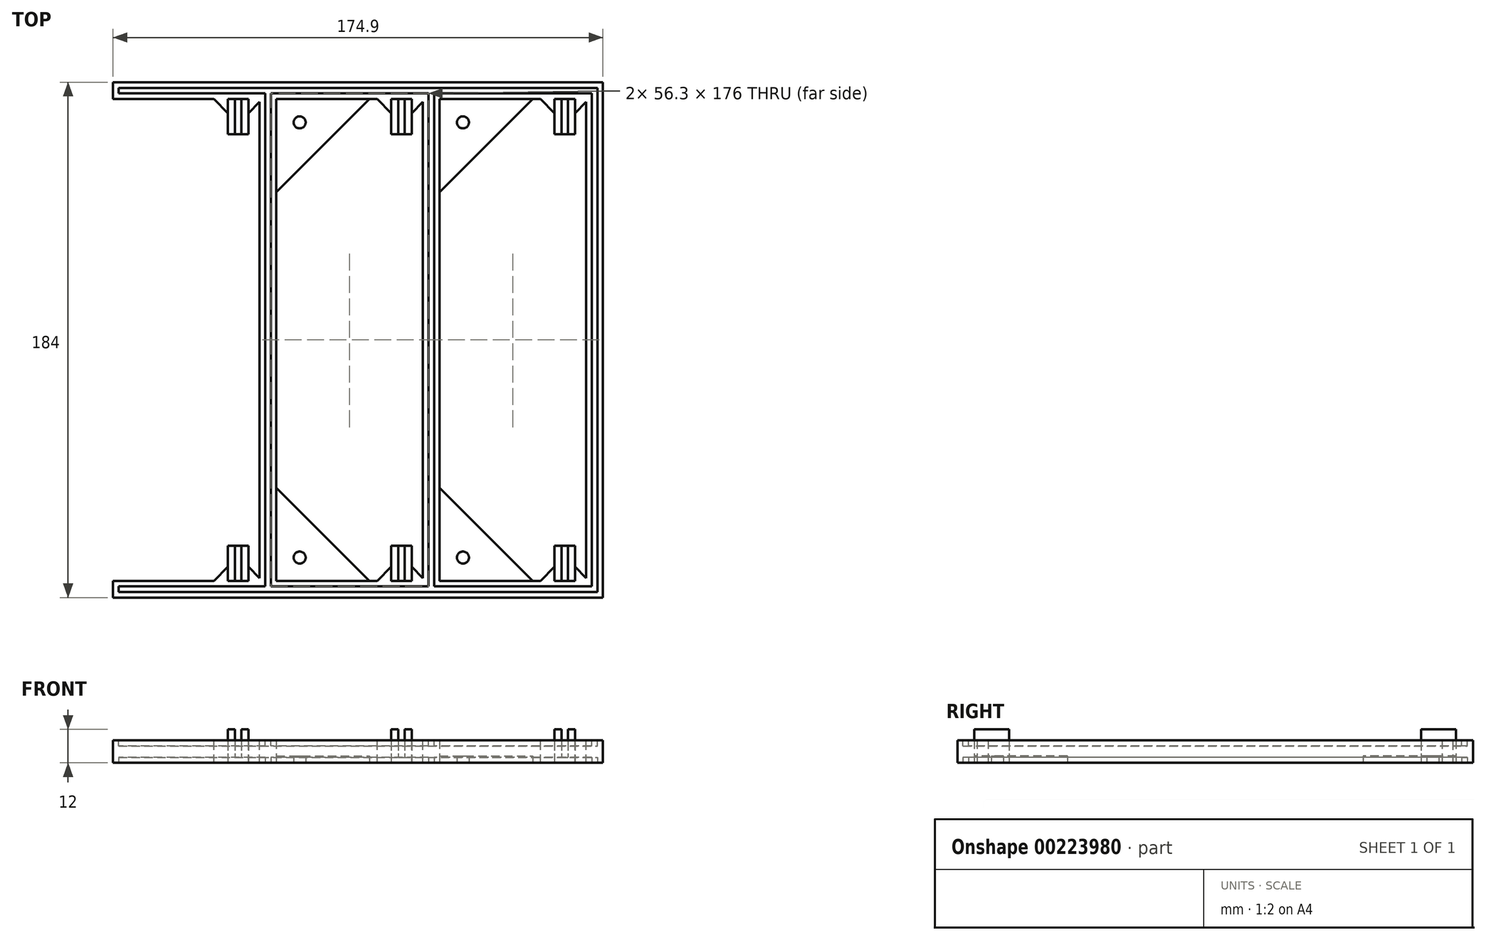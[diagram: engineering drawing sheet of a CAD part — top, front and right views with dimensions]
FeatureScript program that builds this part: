
annotation { "Feature Type Name" : "Feature", "Feature Type Description" : "" }
export const myFeature = defineFeature(function(context is Context, id is Id, definition is map)
    precondition{}
    {
        {
            var Q0;
            Q0=qCreatedBy(makeId("Top.planeOp"),FACE);
            var sketch = newSketch(context, id + "F0", { "sketchPlane" : qUnion([Q0])});
            skLineSegment(sketch, "E0", {"start": v(-87.45, 92) * mm, "end": v(87.45, 92) * mm});
            skLineSegment(sketch, "E1", {"start": v(-46.45, 73.5) * mm, "end": v(-43.95, 73.5) * mm});
            skLineSegment(sketch, "E2", {"start": v(-43.95, 73.5) * mm, "end": v(-43.95, 86) * mm});
            skLineSegment(sketch, "E3", {"start": v(-43.95, 86) * mm, "end": v(-41.65, 86) * mm});
            skLineSegment(sketch, "E4", {"start": v(-41.65, 86) * mm, "end": v(-41.65, 73.5) * mm});
            skLineSegment(sketch, "E5", {"start": v(-41.65, 73.5) * mm, "end": v(-39.15, 73.5) * mm});
            skLineSegment(sketch, "E6", {"start": v(-39.15, 73.5) * mm, "end": v(-39.15, 86) * mm});
            skLineSegment(sketch, "E7", {"start": v(-39.15, 86) * mm, "end": v(-35.15, 86) * mm});
            skLineSegment(sketch, "E8", {"start": v(-35.15, 86) * mm, "end": v(-35.15, 0) * mm});
            skLineSegment(sketch, "E9", {"start": v(-29.15, 0) * mm, "end": v(-29.15, 86) * mm});
            skLineSegment(sketch, "E10", {"start": v(-29.15, 86) * mm, "end": v(11.85, 86) * mm});
            skLineSegment(sketch, "E11", {"start": v(11.85, 86) * mm, "end": v(11.85, 73.5) * mm});
            skLineSegment(sketch, "E12", {"start": v(11.85, 73.5) * mm, "end": v(14.35, 73.5) * mm});
            skLineSegment(sketch, "E13", {"start": v(14.35, 73.5) * mm, "end": v(14.35, 86) * mm});
            skLineSegment(sketch, "E14", {"start": v(14.35, 86) * mm, "end": v(16.65, 86) * mm});
            skLineSegment(sketch, "E15", {"start": v(16.65, 86) * mm, "end": v(16.65, 73.5) * mm});
            skLineSegment(sketch, "E16", {"start": v(16.65, 73.5) * mm, "end": v(19.15, 73.5) * mm});
            skLineSegment(sketch, "E17", {"start": v(19.15, 73.5) * mm, "end": v(19.15, 86) * mm});
            skLineSegment(sketch, "E18", {"start": v(19.15, 86) * mm, "end": v(23.15, 86) * mm});
            skLineSegment(sketch, "E19", {"start": v(23.15, 86) * mm, "end": v(23.15, 0) * mm});
            skLineSegment(sketch, "E20", {"start": v(29.15, 0) * mm, "end": v(29.15, 86) * mm});
            skLineSegment(sketch, "E21", {"start": v(29.15, 86) * mm, "end": v(70.15, 86) * mm});
            skLineSegment(sketch, "E22", {"start": v(70.15, 86) * mm, "end": v(70.15, 73.5) * mm});
            skLineSegment(sketch, "E23", {"start": v(70.15, 73.5) * mm, "end": v(72.65, 73.5) * mm});
            skLineSegment(sketch, "E24", {"start": v(72.65, 73.5) * mm, "end": v(72.65, 86) * mm});
            skLineSegment(sketch, "E25", {"start": v(72.65, 86) * mm, "end": v(74.95, 86) * mm});
            skLineSegment(sketch, "E26", {"start": v(74.95, 86) * mm, "end": v(74.95, 73.5) * mm});
            skLineSegment(sketch, "E27", {"start": v(74.95, 73.5) * mm, "end": v(77.45, 73.5) * mm});
            skLineSegment(sketch, "E28", {"start": v(77.45, 73.5) * mm, "end": v(77.45, 86) * mm});
            skLineSegment(sketch, "E29", {"start": v(77.45, 86) * mm, "end": v(81.45, 86) * mm});
            skLineSegment(sketch, "E30", {"start": v(81.45, 86) * mm, "end": v(81.45, 0) * mm});
            skLineSegment(sketch, "E31", {"start": v(87.45, 0) * mm, "end": v(87.45, 92) * mm});
            skLineSegment(sketch, "E32", {"start": v(-8.65, 86) * mm, "end": v(-8.65, 92) * mm, "construction": true});
            skPoint(sketch, "E33", {"position": v(0, 92) * mm});
            skLineSegment(sketch, "E34", {"start": v(-35.15, 43) * mm, "end": v(-29.15, 43) * mm, "construction": true});
            skLineSegment(sketch, "E35", {"start": v(23.15, 43) * mm, "end": v(29.15, 43) * mm, "construction": true});
            skLineSegment(sketch, "E36", {"start": v(81.45, 43) * mm, "end": v(87.45, 43) * mm, "construction": true});
            skLineSegment(sketch, "E37", {"start": v(-46.45, 73.5) * mm, "end": v(-46.45, 86) * mm});
            skLineSegment(sketch, "E38", {"start": v(-46.45, 86) * mm, "end": v(-87.45, 86) * mm});
            skLineSegment(sketch, "E39", {"start": v(-87.45, 86) * mm, "end": v(-87.45, 92) * mm});
            skLineSegment(sketch, "E40.MirrorCS", {"start": v(74.95, -73.5) * mm, "end": v(77.45, -73.5) * mm});
            skLineSegment(sketch, "E41.MirrorCS", {"start": v(77.45, -86) * mm, "end": v(81.45, -86) * mm});
            skLineSegment(sketch, "E42.MirrorCS", {"start": v(19.15, -86) * mm, "end": v(23.15, -86) * mm});
            skLineSegment(sketch, "E43.MirrorCS", {"start": v(11.85, -73.5) * mm, "end": v(14.35, -73.5) * mm});
            skLineSegment(sketch, "E44.MirrorCS", {"start": v(70.15, -73.5) * mm, "end": v(72.65, -73.5) * mm});
            skLineSegment(sketch, "E45.MirrorCS", {"start": v(-46.45, -73.5) * mm, "end": v(-43.95, -73.5) * mm});
            skLineSegment(sketch, "E46.MirrorCS", {"start": v(-43.95, -86) * mm, "end": v(-41.65, -86) * mm});
            skLineSegment(sketch, "E47.MirrorCS", {"start": v(-41.65, -73.5) * mm, "end": v(-39.15, -73.5) * mm});
            skLineSegment(sketch, "E48.MirrorCS", {"start": v(-39.15, -86) * mm, "end": v(-35.15, -86) * mm});
            skLineSegment(sketch, "E49.MirrorCS", {"start": v(72.65, -86) * mm, "end": v(74.95, -86) * mm});
            skLineSegment(sketch, "E50.MirrorCS", {"start": v(16.65, -73.5) * mm, "end": v(19.15, -73.5) * mm});
            skLineSegment(sketch, "E51.MirrorCS", {"start": v(14.35, -86) * mm, "end": v(16.65, -86) * mm});
            skLineSegment(sketch, "E52.MirrorCS", {"start": v(29.15, -86) * mm, "end": v(70.15, -86) * mm});
            skLineSegment(sketch, "E53.MirrorCS", {"start": v(-46.45, -73.5) * mm, "end": v(-46.45, -86) * mm});
            skLineSegment(sketch, "E54.MirrorCS", {"start": v(19.15, -73.5) * mm, "end": v(19.15, -86) * mm});
            skLineSegment(sketch, "E55.MirrorCS", {"start": v(-43.95, -73.5) * mm, "end": v(-43.95, -86) * mm});
            skLineSegment(sketch, "E56.MirrorCS", {"start": v(87.45, 0) * mm, "end": v(87.45, -92) * mm});
            skLineSegment(sketch, "E57.MirrorCS", {"start": v(-87.45, -86) * mm, "end": v(-87.45, -92) * mm});
            skLineSegment(sketch, "E58.MirrorCS", {"start": v(29.15, 0) * mm, "end": v(29.15, -86) * mm});
            skPoint(sketch, "E59.MirrorP", {"position": v(0, -92) * mm});
            skLineSegment(sketch, "E60.MirrorCS", {"start": v(-8.65, -86) * mm, "end": v(-8.65, -92) * mm, "construction": true});
            skLineSegment(sketch, "E61.MirrorCS", {"start": v(72.65, -73.5) * mm, "end": v(72.65, -86) * mm});
            skLineSegment(sketch, "E62.MirrorCS", {"start": v(81.45, -86) * mm, "end": v(81.45, 0) * mm});
            skLineSegment(sketch, "E63.MirrorCS", {"start": v(23.15, -86) * mm, "end": v(23.15, 0) * mm});
            skLineSegment(sketch, "E64.MirrorCS", {"start": v(-46.45, -86) * mm, "end": v(-87.45, -86) * mm});
            skLineSegment(sketch, "E65.MirrorCS", {"start": v(-87.45, -92) * mm, "end": v(87.45, -92) * mm});
            skLineSegment(sketch, "E66.MirrorCS", {"start": v(70.15, -86) * mm, "end": v(70.15, -73.5) * mm});
            skLineSegment(sketch, "E67.MirrorCS", {"start": v(-41.65, -86) * mm, "end": v(-41.65, -73.5) * mm});
            skLineSegment(sketch, "E68.MirrorCS", {"start": v(-39.15, -73.5) * mm, "end": v(-39.15, -86) * mm});
            skLineSegment(sketch, "E69.MirrorCS", {"start": v(-35.15, -86) * mm, "end": v(-35.15, 0) * mm});
            skLineSegment(sketch, "E70.MirrorCS", {"start": v(-29.15, 0) * mm, "end": v(-29.15, -86) * mm});
            skLineSegment(sketch, "E71.MirrorCS", {"start": v(-29.15, -86) * mm, "end": v(11.85, -86) * mm});
            skLineSegment(sketch, "E72.MirrorCS", {"start": v(11.85, -86) * mm, "end": v(11.85, -73.5) * mm});
            skLineSegment(sketch, "E73.MirrorCS", {"start": v(77.45, -73.5) * mm, "end": v(77.45, -86) * mm});
            skLineSegment(sketch, "E74.MirrorCS", {"start": v(74.95, -86) * mm, "end": v(74.95, -73.5) * mm});
            skLineSegment(sketch, "E75.MirrorCS", {"start": v(14.35, -73.5) * mm, "end": v(14.35, -86) * mm});
            skLineSegment(sketch, "E76.MirrorCS", {"start": v(16.65, -86) * mm, "end": v(16.65, -73.5) * mm});
            skSolve(sketch);
        }
        {
            var Q0;
            Q0=qSketchRegion(id+"F0",true);
            extrude(context, id + "F1", {"entities" : qUnion([Q0]), "depth" : 8 * mm});
        }
        {
            var Q0;
            Q0=makeQuery(id+"F1.opExtrude","CAP_FACE",FACE,{"disambiguationData":[OSD([sQuery(id+"F0.wireOp",EDGE,"E0"),sQuery(id+"F0.wireOp",EDGE,"E1"),sQuery(id+"F0.wireOp",EDGE,"E2"),sQuery(id+"F0.wireOp",EDGE,"E3"),sQuery(id+"F0.wireOp",EDGE,"E4"),sQuery(id+"F0.wireOp",EDGE,"E5"),sQuery(id+"F0.wireOp",EDGE,"E6"),sQuery(id+"F0.wireOp",EDGE,"E7"),sQuery(id+"F0.wireOp",EDGE,"E8"),sQuery(id+"F0.wireOp",EDGE,"E9"),sQuery(id+"F0.wireOp",EDGE,"E10"),sQuery(id+"F0.wireOp",EDGE,"E11"),sQuery(id+"F0.wireOp",EDGE,"E12"),sQuery(id+"F0.wireOp",EDGE,"E13"),sQuery(id+"F0.wireOp",EDGE,"E14"),sQuery(id+"F0.wireOp",EDGE,"E15"),sQuery(id+"F0.wireOp",EDGE,"E16"),sQuery(id+"F0.wireOp",EDGE,"E17"),sQuery(id+"F0.wireOp",EDGE,"E18"),sQuery(id+"F0.wireOp",EDGE,"E19"),sQuery(id+"F0.wireOp",EDGE,"E20"),sQuery(id+"F0.wireOp",EDGE,"E21"),sQuery(id+"F0.wireOp",EDGE,"E22"),sQuery(id+"F0.wireOp",EDGE,"E23"),sQuery(id+"F0.wireOp",EDGE,"E24"),sQuery(id+"F0.wireOp",EDGE,"E25"),sQuery(id+"F0.wireOp",EDGE,"E26"),sQuery(id+"F0.wireOp",EDGE,"E27"),sQuery(id+"F0.wireOp",EDGE,"E28"),sQuery(id+"F0.wireOp",EDGE,"E29"),sQuery(id+"F0.wireOp",EDGE,"E30"),sQuery(id+"F0.wireOp",EDGE,"E31"),sQuery(id+"F0.wireOp",EDGE,"E37"),sQuery(id+"F0.wireOp",EDGE,"E38"),sQuery(id+"F0.wireOp",EDGE,"E39"),sQuery(id+"F0.wireOp",EDGE,"E40.MirrorCS"),sQuery(id+"F0.wireOp",EDGE,"E41.MirrorCS"),sQuery(id+"F0.wireOp",EDGE,"E42.MirrorCS"),sQuery(id+"F0.wireOp",EDGE,"E43.MirrorCS"),sQuery(id+"F0.wireOp",EDGE,"E44.MirrorCS"),sQuery(id+"F0.wireOp",EDGE,"E45.MirrorCS"),sQuery(id+"F0.wireOp",EDGE,"E46.MirrorCS"),sQuery(id+"F0.wireOp",EDGE,"E47.MirrorCS"),sQuery(id+"F0.wireOp",EDGE,"E48.MirrorCS"),sQuery(id+"F0.wireOp",EDGE,"E49.MirrorCS"),sQuery(id+"F0.wireOp",EDGE,"E50.MirrorCS"),sQuery(id+"F0.wireOp",EDGE,"E51.MirrorCS"),sQuery(id+"F0.wireOp",EDGE,"E52.MirrorCS"),sQuery(id+"F0.wireOp",EDGE,"E53.MirrorCS"),sQuery(id+"F0.wireOp",EDGE,"E54.MirrorCS"),sQuery(id+"F0.wireOp",EDGE,"E55.MirrorCS"),sQuery(id+"F0.wireOp",EDGE,"E56.MirrorCS"),sQuery(id+"F0.wireOp",EDGE,"E57.MirrorCS"),sQuery(id+"F0.wireOp",EDGE,"E58.MirrorCS"),sQuery(id+"F0.wireOp",EDGE,"E61.MirrorCS"),sQuery(id+"F0.wireOp",EDGE,"E62.MirrorCS"),sQuery(id+"F0.wireOp",EDGE,"E63.MirrorCS"),sQuery(id+"F0.wireOp",EDGE,"E64.MirrorCS"),sQuery(id+"F0.wireOp",EDGE,"E65.MirrorCS"),sQuery(id+"F0.wireOp",EDGE,"E66.MirrorCS"),sQuery(id+"F0.wireOp",EDGE,"E67.MirrorCS"),sQuery(id+"F0.wireOp",EDGE,"E68.MirrorCS"),sQuery(id+"F0.wireOp",EDGE,"E69.MirrorCS"),sQuery(id+"F0.wireOp",EDGE,"E70.MirrorCS"),sQuery(id+"F0.wireOp",EDGE,"E71.MirrorCS"),sQuery(id+"F0.wireOp",EDGE,"E72.MirrorCS"),sQuery(id+"F0.wireOp",EDGE,"E73.MirrorCS"),sQuery(id+"F0.wireOp",EDGE,"E74.MirrorCS"),sQuery(id+"F0.wireOp",EDGE,"E75.MirrorCS"),sQuery(id+"F0.wireOp",EDGE,"E76.MirrorCS")])],"isStart":false});
            var sketch = newSketch(context, id + "F2", { "sketchPlane" : qUnion([Q0])});
            skLineSegment(sketch, "E77.0", {"start": v(-46.45, 73.5) * mm, "end": v(-46.45, 86) * mm});
            skLineSegment(sketch, "E77.1", {"start": v(-46.45, 73.5) * mm, "end": v(-43.95, 73.5) * mm});
            skLineSegment(sketch, "E77.2", {"start": v(-43.95, 73.5) * mm, "end": v(-43.95, 86) * mm});
            skLineSegment(sketch, "E77.3", {"start": v(-41.65, 86) * mm, "end": v(-41.65, 73.5) * mm});
            skLineSegment(sketch, "E77.4", {"start": v(-41.65, 73.5) * mm, "end": v(-39.15, 73.5) * mm});
            skLineSegment(sketch, "E77.5", {"start": v(-39.15, 73.5) * mm, "end": v(-39.15, 86) * mm});
            skLineSegment(sketch, "E77.6", {"start": v(-43.95, 86) * mm, "end": v(-41.65, 86) * mm});
            skLineSegment(sketch, "E77.7", {"start": v(11.85, 86) * mm, "end": v(11.85, 73.5) * mm});
            skLineSegment(sketch, "E77.8", {"start": v(14.35, 73.5) * mm, "end": v(14.35, 86) * mm});
            skLineSegment(sketch, "E77.9", {"start": v(16.65, 86) * mm, "end": v(16.65, 73.5) * mm});
            skLineSegment(sketch, "E77.10", {"start": v(14.35, 86) * mm, "end": v(16.65, 86) * mm});
            skLineSegment(sketch, "E77.11", {"start": v(19.15, 73.5) * mm, "end": v(19.15, 86) * mm});
            skLineSegment(sketch, "E77.12", {"start": v(16.65, 73.5) * mm, "end": v(19.15, 73.5) * mm});
            skLineSegment(sketch, "E77.13", {"start": v(11.85, 73.5) * mm, "end": v(14.35, 73.5) * mm});
            skLineSegment(sketch, "E77.14", {"start": v(77.45, 73.5) * mm, "end": v(77.45, 86) * mm});
            skLineSegment(sketch, "E77.15", {"start": v(74.95, 73.5) * mm, "end": v(77.45, 73.5) * mm});
            skLineSegment(sketch, "E77.16", {"start": v(74.95, 86) * mm, "end": v(74.95, 73.5) * mm});
            skLineSegment(sketch, "E77.17", {"start": v(72.65, 86) * mm, "end": v(74.95, 86) * mm});
            skLineSegment(sketch, "E77.18", {"start": v(72.65, 73.5) * mm, "end": v(72.65, 86) * mm});
            skLineSegment(sketch, "E77.19", {"start": v(70.15, 73.5) * mm, "end": v(72.65, 73.5) * mm});
            skLineSegment(sketch, "E77.20", {"start": v(70.15, 86) * mm, "end": v(70.15, 73.5) * mm});
            skLineSegment(sketch, "E78", {"start": v(-46.45, 86) * mm, "end": v(-43.95, 86) * mm});
            skLineSegment(sketch, "E79", {"start": v(-41.65, 86) * mm, "end": v(-39.15, 86) * mm});
            skLineSegment(sketch, "E80", {"start": v(11.85, 86) * mm, "end": v(14.35, 86) * mm});
            skLineSegment(sketch, "E81", {"start": v(16.65, 86) * mm, "end": v(19.15, 86) * mm});
            skLineSegment(sketch, "E82", {"start": v(70.15, 86) * mm, "end": v(72.65, 86) * mm});
            skLineSegment(sketch, "E83", {"start": v(74.95, 86) * mm, "end": v(77.45, 86) * mm});
            skLineSegment(sketch, "E84.MirrorCS", {"start": v(72.65, -86) * mm, "end": v(74.95, -86) * mm});
            skLineSegment(sketch, "E85.MirrorCS", {"start": v(-43.95, -86) * mm, "end": v(-41.65, -86) * mm});
            skLineSegment(sketch, "E86.MirrorCS", {"start": v(14.35, -86) * mm, "end": v(16.65, -86) * mm});
            skLineSegment(sketch, "E87.MirrorCS", {"start": v(70.15, -73.5) * mm, "end": v(72.65, -73.5) * mm});
            skLineSegment(sketch, "E88.MirrorCS", {"start": v(74.95, -73.5) * mm, "end": v(77.45, -73.5) * mm});
            skLineSegment(sketch, "E89.MirrorCS", {"start": v(-41.65, -73.5) * mm, "end": v(-39.15, -73.5) * mm});
            skLineSegment(sketch, "E90.MirrorCS", {"start": v(16.65, -86) * mm, "end": v(19.15, -86) * mm});
            skLineSegment(sketch, "E91.MirrorCS", {"start": v(-46.45, -86) * mm, "end": v(-43.95, -86) * mm});
            skLineSegment(sketch, "E92.MirrorCS", {"start": v(16.65, -73.5) * mm, "end": v(19.15, -73.5) * mm});
            skLineSegment(sketch, "E93.MirrorCS", {"start": v(11.85, -86) * mm, "end": v(14.35, -86) * mm});
            skLineSegment(sketch, "E94.MirrorCS", {"start": v(74.95, -86) * mm, "end": v(77.45, -86) * mm});
            skLineSegment(sketch, "E95.MirrorCS", {"start": v(-46.45, -73.5) * mm, "end": v(-43.95, -73.5) * mm});
            skLineSegment(sketch, "E96.MirrorCS", {"start": v(-41.65, -86) * mm, "end": v(-39.15, -86) * mm});
            skLineSegment(sketch, "E97.MirrorCS", {"start": v(70.15, -86) * mm, "end": v(72.65, -86) * mm});
            skLineSegment(sketch, "E98.MirrorCS", {"start": v(11.85, -73.5) * mm, "end": v(14.35, -73.5) * mm});
            skLineSegment(sketch, "E99.MirrorCS", {"start": v(72.65, -73.5) * mm, "end": v(72.65, -86) * mm});
            skLineSegment(sketch, "E100.MirrorCS", {"start": v(70.15, -86) * mm, "end": v(70.15, -73.5) * mm});
            skLineSegment(sketch, "E101.MirrorCS", {"start": v(77.45, -73.5) * mm, "end": v(77.45, -86) * mm});
            skLineSegment(sketch, "E102.MirrorCS", {"start": v(11.85, -86) * mm, "end": v(11.85, -73.5) * mm});
            skLineSegment(sketch, "E103.MirrorCS", {"start": v(-46.45, -73.5) * mm, "end": v(-46.45, -86) * mm});
            skLineSegment(sketch, "E104.MirrorCS", {"start": v(-43.95, -73.5) * mm, "end": v(-43.95, -86) * mm});
            skLineSegment(sketch, "E105.MirrorCS", {"start": v(74.95, -86) * mm, "end": v(74.95, -73.5) * mm});
            skLineSegment(sketch, "E106.MirrorCS", {"start": v(-41.65, -86) * mm, "end": v(-41.65, -73.5) * mm});
            skLineSegment(sketch, "E107.MirrorCS", {"start": v(14.35, -73.5) * mm, "end": v(14.35, -86) * mm});
            skLineSegment(sketch, "E108.MirrorCS", {"start": v(-39.15, -73.5) * mm, "end": v(-39.15, -86) * mm});
            skLineSegment(sketch, "E109.MirrorCS", {"start": v(19.15, -73.5) * mm, "end": v(19.15, -86) * mm});
            skLineSegment(sketch, "E110.MirrorCS", {"start": v(16.65, -86) * mm, "end": v(16.65, -73.5) * mm});
            skSolve(sketch);
        }
        {
            var Q0;
            Q0=qSketchRegion(id+"F2",true);
            extrude(context, id + "F3", {"entities" : qUnion([Q0]), "operationType" : NewBodyOperationType.ADD, "depth" : 4 * mm});
        }
        {
            var Q0;
            Q0=makeQuery(id+"F1.opExtrude","CAP_FACE",FACE,{"disambiguationData":[OSD([sQuery(id+"F0.wireOp",EDGE,"E0"),sQuery(id+"F0.wireOp",EDGE,"E1"),sQuery(id+"F0.wireOp",EDGE,"E2"),sQuery(id+"F0.wireOp",EDGE,"E3"),sQuery(id+"F0.wireOp",EDGE,"E4"),sQuery(id+"F0.wireOp",EDGE,"E5"),sQuery(id+"F0.wireOp",EDGE,"E6"),sQuery(id+"F0.wireOp",EDGE,"E7"),sQuery(id+"F0.wireOp",EDGE,"E8"),sQuery(id+"F0.wireOp",EDGE,"E9"),sQuery(id+"F0.wireOp",EDGE,"E10"),sQuery(id+"F0.wireOp",EDGE,"E11"),sQuery(id+"F0.wireOp",EDGE,"E12"),sQuery(id+"F0.wireOp",EDGE,"E13"),sQuery(id+"F0.wireOp",EDGE,"E14"),sQuery(id+"F0.wireOp",EDGE,"E15"),sQuery(id+"F0.wireOp",EDGE,"E16"),sQuery(id+"F0.wireOp",EDGE,"E17"),sQuery(id+"F0.wireOp",EDGE,"E18"),sQuery(id+"F0.wireOp",EDGE,"E19"),sQuery(id+"F0.wireOp",EDGE,"E20"),sQuery(id+"F0.wireOp",EDGE,"E21"),sQuery(id+"F0.wireOp",EDGE,"E22"),sQuery(id+"F0.wireOp",EDGE,"E23"),sQuery(id+"F0.wireOp",EDGE,"E24"),sQuery(id+"F0.wireOp",EDGE,"E25"),sQuery(id+"F0.wireOp",EDGE,"E26"),sQuery(id+"F0.wireOp",EDGE,"E27"),sQuery(id+"F0.wireOp",EDGE,"E28"),sQuery(id+"F0.wireOp",EDGE,"E29"),sQuery(id+"F0.wireOp",EDGE,"E30"),sQuery(id+"F0.wireOp",EDGE,"E31"),sQuery(id+"F0.wireOp",EDGE,"E37"),sQuery(id+"F0.wireOp",EDGE,"E38"),sQuery(id+"F0.wireOp",EDGE,"E39"),sQuery(id+"F0.wireOp",EDGE,"E40.MirrorCS"),sQuery(id+"F0.wireOp",EDGE,"E41.MirrorCS"),sQuery(id+"F0.wireOp",EDGE,"E42.MirrorCS"),sQuery(id+"F0.wireOp",EDGE,"E43.MirrorCS"),sQuery(id+"F0.wireOp",EDGE,"E44.MirrorCS"),sQuery(id+"F0.wireOp",EDGE,"E45.MirrorCS"),sQuery(id+"F0.wireOp",EDGE,"E46.MirrorCS"),sQuery(id+"F0.wireOp",EDGE,"E47.MirrorCS"),sQuery(id+"F0.wireOp",EDGE,"E48.MirrorCS"),sQuery(id+"F0.wireOp",EDGE,"E49.MirrorCS"),sQuery(id+"F0.wireOp",EDGE,"E50.MirrorCS"),sQuery(id+"F0.wireOp",EDGE,"E51.MirrorCS"),sQuery(id+"F0.wireOp",EDGE,"E52.MirrorCS"),sQuery(id+"F0.wireOp",EDGE,"E53.MirrorCS"),sQuery(id+"F0.wireOp",EDGE,"E54.MirrorCS"),sQuery(id+"F0.wireOp",EDGE,"E55.MirrorCS"),sQuery(id+"F0.wireOp",EDGE,"E56.MirrorCS"),sQuery(id+"F0.wireOp",EDGE,"E57.MirrorCS"),sQuery(id+"F0.wireOp",EDGE,"E58.MirrorCS"),sQuery(id+"F0.wireOp",EDGE,"E61.MirrorCS"),sQuery(id+"F0.wireOp",EDGE,"E62.MirrorCS"),sQuery(id+"F0.wireOp",EDGE,"E63.MirrorCS"),sQuery(id+"F0.wireOp",EDGE,"E64.MirrorCS"),sQuery(id+"F0.wireOp",EDGE,"E65.MirrorCS"),sQuery(id+"F0.wireOp",EDGE,"E66.MirrorCS"),sQuery(id+"F0.wireOp",EDGE,"E67.MirrorCS"),sQuery(id+"F0.wireOp",EDGE,"E68.MirrorCS"),sQuery(id+"F0.wireOp",EDGE,"E69.MirrorCS"),sQuery(id+"F0.wireOp",EDGE,"E70.MirrorCS"),sQuery(id+"F0.wireOp",EDGE,"E71.MirrorCS"),sQuery(id+"F0.wireOp",EDGE,"E72.MirrorCS"),sQuery(id+"F0.wireOp",EDGE,"E73.MirrorCS"),sQuery(id+"F0.wireOp",EDGE,"E74.MirrorCS"),sQuery(id+"F0.wireOp",EDGE,"E75.MirrorCS"),sQuery(id+"F0.wireOp",EDGE,"E76.MirrorCS")])],"isStart":true});
            var sketch = newSketch(context, id + "F4", { "sketchPlane" : qUnion([Q0])});
            skLineSegment(sketch, "E111.bottom", {"start": v(-46.45, 73.5) * mm, "end": v(-39.15, 73.5) * mm});
            skLineSegment(sketch, "E111.top", {"start": v(-46.45, 86) * mm, "end": v(-39.15, 86) * mm});
            skLineSegment(sketch, "E111.left", {"start": v(-46.45, 73.5) * mm, "end": v(-46.45, 86) * mm});
            skLineSegment(sketch, "E111.right", {"start": v(-39.15, 73.5) * mm, "end": v(-39.15, 86) * mm});
            skLineSegment(sketch, "E112.bottom", {"start": v(11.85, 73.5) * mm, "end": v(19.15, 73.5) * mm});
            skLineSegment(sketch, "E112.top", {"start": v(11.85, 86) * mm, "end": v(19.15, 86) * mm});
            skLineSegment(sketch, "E112.left", {"start": v(11.85, 73.5) * mm, "end": v(11.85, 86) * mm});
            skLineSegment(sketch, "E112.right", {"start": v(19.15, 73.5) * mm, "end": v(19.15, 86) * mm});
            skLineSegment(sketch, "E113.bottom", {"start": v(70.15, 73.5) * mm, "end": v(77.45, 73.5) * mm});
            skLineSegment(sketch, "E113.top", {"start": v(70.15, 86) * mm, "end": v(77.45, 86) * mm});
            skLineSegment(sketch, "E113.left", {"start": v(70.15, 73.5) * mm, "end": v(70.15, 86) * mm});
            skLineSegment(sketch, "E113.right", {"start": v(77.45, 73.5) * mm, "end": v(77.45, 86) * mm});
            skLineSegment(sketch, "E114.MirrorCS", {"start": v(11.85, -86) * mm, "end": v(19.15, -86) * mm});
            skLineSegment(sketch, "E115.MirrorCS", {"start": v(11.85, -73.5) * mm, "end": v(19.15, -73.5) * mm});
            skLineSegment(sketch, "E116.MirrorCS", {"start": v(-39.15, -73.5) * mm, "end": v(-39.15, -86) * mm});
            skLineSegment(sketch, "E117.MirrorCS", {"start": v(11.85, -73.5) * mm, "end": v(11.85, -86) * mm});
            skLineSegment(sketch, "E118.MirrorCS", {"start": v(70.15, -73.5) * mm, "end": v(70.15, -86) * mm});
            skLineSegment(sketch, "E119.MirrorCS", {"start": v(77.45, -73.5) * mm, "end": v(77.45, -86) * mm});
            skLineSegment(sketch, "E120.MirrorCS", {"start": v(19.15, -73.5) * mm, "end": v(19.15, -86) * mm});
            skLineSegment(sketch, "E121.MirrorCS", {"start": v(70.15, -86) * mm, "end": v(77.45, -86) * mm});
            skLineSegment(sketch, "E122.MirrorCS", {"start": v(-46.45, -73.5) * mm, "end": v(-46.45, -86) * mm});
            skLineSegment(sketch, "E123.MirrorCS", {"start": v(-46.45, -73.5) * mm, "end": v(-39.15, -73.5) * mm});
            skLineSegment(sketch, "E124.MirrorCS", {"start": v(-46.45, -86) * mm, "end": v(-39.15, -86) * mm});
            skLineSegment(sketch, "E125.MirrorCS", {"start": v(70.15, -73.5) * mm, "end": v(77.45, -73.5) * mm});
            skSolve(sketch);
        }
        {
            var Q0;
            Q0=qSketchRegion(id+"F4",true);
            extrude(context, id + "F5", {"entities" : qUnion([Q0]), "operationType" : NewBodyOperationType.ADD, "oppositeDirection" : true, "depth" : 2 * mm});
        }
        {
            var Q0;
            Q0=makeQuery(id+"F1.opExtrude","CAP_FACE",FACE,{"disambiguationData":[OSD([sQuery(id+"F0.wireOp",EDGE,"E0"),sQuery(id+"F0.wireOp",EDGE,"E1"),sQuery(id+"F0.wireOp",EDGE,"E2"),sQuery(id+"F0.wireOp",EDGE,"E3"),sQuery(id+"F0.wireOp",EDGE,"E4"),sQuery(id+"F0.wireOp",EDGE,"E5"),sQuery(id+"F0.wireOp",EDGE,"E6"),sQuery(id+"F0.wireOp",EDGE,"E7"),sQuery(id+"F0.wireOp",EDGE,"E8"),sQuery(id+"F0.wireOp",EDGE,"E9"),sQuery(id+"F0.wireOp",EDGE,"E10"),sQuery(id+"F0.wireOp",EDGE,"E11"),sQuery(id+"F0.wireOp",EDGE,"E12"),sQuery(id+"F0.wireOp",EDGE,"E13"),sQuery(id+"F0.wireOp",EDGE,"E14"),sQuery(id+"F0.wireOp",EDGE,"E15"),sQuery(id+"F0.wireOp",EDGE,"E16"),sQuery(id+"F0.wireOp",EDGE,"E17"),sQuery(id+"F0.wireOp",EDGE,"E18"),sQuery(id+"F0.wireOp",EDGE,"E19"),sQuery(id+"F0.wireOp",EDGE,"E20"),sQuery(id+"F0.wireOp",EDGE,"E21"),sQuery(id+"F0.wireOp",EDGE,"E22"),sQuery(id+"F0.wireOp",EDGE,"E23"),sQuery(id+"F0.wireOp",EDGE,"E24"),sQuery(id+"F0.wireOp",EDGE,"E25"),sQuery(id+"F0.wireOp",EDGE,"E26"),sQuery(id+"F0.wireOp",EDGE,"E27"),sQuery(id+"F0.wireOp",EDGE,"E28"),sQuery(id+"F0.wireOp",EDGE,"E29"),sQuery(id+"F0.wireOp",EDGE,"E30"),sQuery(id+"F0.wireOp",EDGE,"E31"),sQuery(id+"F0.wireOp",EDGE,"E37"),sQuery(id+"F0.wireOp",EDGE,"E38"),sQuery(id+"F0.wireOp",EDGE,"E39"),sQuery(id+"F0.wireOp",EDGE,"E40.MirrorCS"),sQuery(id+"F0.wireOp",EDGE,"E41.MirrorCS"),sQuery(id+"F0.wireOp",EDGE,"E42.MirrorCS"),sQuery(id+"F0.wireOp",EDGE,"E43.MirrorCS"),sQuery(id+"F0.wireOp",EDGE,"E44.MirrorCS"),sQuery(id+"F0.wireOp",EDGE,"E45.MirrorCS"),sQuery(id+"F0.wireOp",EDGE,"E46.MirrorCS"),sQuery(id+"F0.wireOp",EDGE,"E47.MirrorCS"),sQuery(id+"F0.wireOp",EDGE,"E48.MirrorCS"),sQuery(id+"F0.wireOp",EDGE,"E49.MirrorCS"),sQuery(id+"F0.wireOp",EDGE,"E50.MirrorCS"),sQuery(id+"F0.wireOp",EDGE,"E51.MirrorCS"),sQuery(id+"F0.wireOp",EDGE,"E52.MirrorCS"),sQuery(id+"F0.wireOp",EDGE,"E53.MirrorCS"),sQuery(id+"F0.wireOp",EDGE,"E54.MirrorCS"),sQuery(id+"F0.wireOp",EDGE,"E55.MirrorCS"),sQuery(id+"F0.wireOp",EDGE,"E56.MirrorCS"),sQuery(id+"F0.wireOp",EDGE,"E57.MirrorCS"),sQuery(id+"F0.wireOp",EDGE,"E58.MirrorCS"),sQuery(id+"F0.wireOp",EDGE,"E61.MirrorCS"),sQuery(id+"F0.wireOp",EDGE,"E62.MirrorCS"),sQuery(id+"F0.wireOp",EDGE,"E63.MirrorCS"),sQuery(id+"F0.wireOp",EDGE,"E64.MirrorCS"),sQuery(id+"F0.wireOp",EDGE,"E65.MirrorCS"),sQuery(id+"F0.wireOp",EDGE,"E66.MirrorCS"),sQuery(id+"F0.wireOp",EDGE,"E67.MirrorCS"),sQuery(id+"F0.wireOp",EDGE,"E68.MirrorCS"),sQuery(id+"F0.wireOp",EDGE,"E69.MirrorCS"),sQuery(id+"F0.wireOp",EDGE,"E70.MirrorCS"),sQuery(id+"F0.wireOp",EDGE,"E71.MirrorCS"),sQuery(id+"F0.wireOp",EDGE,"E72.MirrorCS"),sQuery(id+"F0.wireOp",EDGE,"E73.MirrorCS"),sQuery(id+"F0.wireOp",EDGE,"E74.MirrorCS"),sQuery(id+"F0.wireOp",EDGE,"E75.MirrorCS"),sQuery(id+"F0.wireOp",EDGE,"E76.MirrorCS")])],"isStart":false});
            var sketch = newSketch(context, id + "F6", { "sketchPlane" : qUnion([Q0])});
            skLineSegment(sketch, "E126", {"start": v(-85.45, 90) * mm, "end": v(85.45, 90) * mm});
            skLineSegment(sketch, "E127", {"start": v(85.45, 90) * mm, "end": v(85.45, 0) * mm});
            skPoint(sketch, "E127.endSnap0", {"position": v(81.45, 0) * mm});
            skLineSegment(sketch, "E128", {"start": v(83.45, 88) * mm, "end": v(83.45, 0) * mm});
            skLineSegment(sketch, "E129", {"start": v(83.45, 88) * mm, "end": v(27.15, 88) * mm});
            skLineSegment(sketch, "E130", {"start": v(27.15, 88) * mm, "end": v(27.15, 0) * mm});
            skPoint(sketch, "E130.endSnap0", {"position": v(29.15, 0) * mm});
            skLineSegment(sketch, "E131", {"start": v(25.15, 0) * mm, "end": v(25.15, 88) * mm});
            skLineSegment(sketch, "E132", {"start": v(25.15, 88) * mm, "end": v(-31.15, 88) * mm});
            skLineSegment(sketch, "E133", {"start": v(-31.15, 88) * mm, "end": v(-31.15, 0) * mm});
            skPoint(sketch, "E133.endSnap0", {"position": v(-29.15, 0) * mm});
            skLineSegment(sketch, "E134", {"start": v(-33.15, 0) * mm, "end": v(-33.15, 88) * mm});
            skLineSegment(sketch, "E135", {"start": v(-33.15, 88) * mm, "end": v(-85.45, 88) * mm});
            skLineSegment(sketch, "E136", {"start": v(-85.45, 90) * mm, "end": v(-85.45, 88) * mm});
            skLineSegment(sketch, "E137", {"start": v(-33.15, 44) * mm, "end": v(-31.15, 44) * mm, "construction": true});
            skLineSegment(sketch, "E138", {"start": v(25.15, 44) * mm, "end": v(27.15, 44) * mm, "construction": true});
            skLineSegment(sketch, "E139", {"start": v(83.45, 44) * mm, "end": v(85.45, 44) * mm, "construction": true});
            skLineSegment(sketch, "E140", {"start": v(0, 90) * mm, "end": v(0, 92) * mm, "construction": true});
            skLineSegment(sketch, "E141", {"start": v(27.15, 44) * mm, "end": v(29.15, 44) * mm, "construction": true});
            skLineSegment(sketch, "E142", {"start": v(85.45, 44) * mm, "end": v(87.45, 44) * mm, "construction": true});
            skLineSegment(sketch, "E143", {"start": v(-31.15, 44) * mm, "end": v(-29.15, 44) * mm, "construction": true});
            skLineSegment(sketch, "E144", {"start": v(-85.45, 89) * mm, "end": v(-87.45, 89) * mm, "construction": true});
            skLineSegment(sketch, "E145.MirrorCS", {"start": v(85.45, -44) * mm, "end": v(87.45, -44) * mm, "construction": true});
            skLineSegment(sketch, "E146.MirrorCS", {"start": v(-85.45, -90) * mm, "end": v(-85.45, -88) * mm});
            skLineSegment(sketch, "E147.MirrorCS", {"start": v(-85.45, -89) * mm, "end": v(-87.45, -89) * mm, "construction": true});
            skLineSegment(sketch, "E148.MirrorCS", {"start": v(-31.15, -44) * mm, "end": v(-29.15, -44) * mm, "construction": true});
            skLineSegment(sketch, "E149.MirrorCS", {"start": v(25.15, -44) * mm, "end": v(27.15, -44) * mm, "construction": true});
            skLineSegment(sketch, "E150.MirrorCS", {"start": v(27.15, -44) * mm, "end": v(29.15, -44) * mm, "construction": true});
            skLineSegment(sketch, "E151.MirrorCS", {"start": v(0, -90) * mm, "end": v(0, -92) * mm, "construction": true});
            skLineSegment(sketch, "E152.MirrorCS", {"start": v(-33.15, -44) * mm, "end": v(-31.15, -44) * mm, "construction": true});
            skLineSegment(sketch, "E153.MirrorCS", {"start": v(83.45, -44) * mm, "end": v(85.45, -44) * mm, "construction": true});
            skLineSegment(sketch, "E154.MirrorCS", {"start": v(27.15, -88) * mm, "end": v(27.15, 0) * mm});
            skLineSegment(sketch, "E155.MirrorCS", {"start": v(83.45, -88) * mm, "end": v(27.15, -88) * mm});
            skLineSegment(sketch, "E156.MirrorCS", {"start": v(25.15, 0) * mm, "end": v(25.15, -88) * mm});
            skLineSegment(sketch, "E157.MirrorCS", {"start": v(25.15, -88) * mm, "end": v(-31.15, -88) * mm});
            skLineSegment(sketch, "E158.MirrorCS", {"start": v(83.45, -88) * mm, "end": v(83.45, 0) * mm});
            skLineSegment(sketch, "E159.MirrorCS", {"start": v(-31.15, -88) * mm, "end": v(-31.15, 0) * mm});
            skLineSegment(sketch, "E160.MirrorCS", {"start": v(-33.15, 0) * mm, "end": v(-33.15, -88) * mm});
            skLineSegment(sketch, "E161.MirrorCS", {"start": v(85.45, -90) * mm, "end": v(85.45, 0) * mm});
            skLineSegment(sketch, "E162.MirrorCS", {"start": v(-85.45, -90) * mm, "end": v(85.45, -90) * mm});
            skLineSegment(sketch, "E163.MirrorCS", {"start": v(-33.15, -88) * mm, "end": v(-85.45, -88) * mm});
            skSolve(sketch);
        }
        {
            var Q0;
            Q0=qSketchRegion(id+"F6",true);
            extrude(context, id + "F7", {"entities" : qUnion([Q0]), "operationType" : NewBodyOperationType.REMOVE, "oppositeDirection" : true, "depth" : 2 * mm});
        }
        {
            var Q0;
            Q0=makeQuery(id+"F1.opExtrude","CAP_FACE",FACE,{"disambiguationData":[OSD([sQuery(id+"F0.wireOp",EDGE,"E0"),sQuery(id+"F0.wireOp",EDGE,"E1"),sQuery(id+"F0.wireOp",EDGE,"E2"),sQuery(id+"F0.wireOp",EDGE,"E3"),sQuery(id+"F0.wireOp",EDGE,"E4"),sQuery(id+"F0.wireOp",EDGE,"E5"),sQuery(id+"F0.wireOp",EDGE,"E6"),sQuery(id+"F0.wireOp",EDGE,"E7"),sQuery(id+"F0.wireOp",EDGE,"E8"),sQuery(id+"F0.wireOp",EDGE,"E9"),sQuery(id+"F0.wireOp",EDGE,"E10"),sQuery(id+"F0.wireOp",EDGE,"E11"),sQuery(id+"F0.wireOp",EDGE,"E12"),sQuery(id+"F0.wireOp",EDGE,"E13"),sQuery(id+"F0.wireOp",EDGE,"E14"),sQuery(id+"F0.wireOp",EDGE,"E15"),sQuery(id+"F0.wireOp",EDGE,"E16"),sQuery(id+"F0.wireOp",EDGE,"E17"),sQuery(id+"F0.wireOp",EDGE,"E18"),sQuery(id+"F0.wireOp",EDGE,"E19"),sQuery(id+"F0.wireOp",EDGE,"E20"),sQuery(id+"F0.wireOp",EDGE,"E21"),sQuery(id+"F0.wireOp",EDGE,"E22"),sQuery(id+"F0.wireOp",EDGE,"E23"),sQuery(id+"F0.wireOp",EDGE,"E24"),sQuery(id+"F0.wireOp",EDGE,"E25"),sQuery(id+"F0.wireOp",EDGE,"E26"),sQuery(id+"F0.wireOp",EDGE,"E27"),sQuery(id+"F0.wireOp",EDGE,"E28"),sQuery(id+"F0.wireOp",EDGE,"E29"),sQuery(id+"F0.wireOp",EDGE,"E30"),sQuery(id+"F0.wireOp",EDGE,"E31"),sQuery(id+"F0.wireOp",EDGE,"E37"),sQuery(id+"F0.wireOp",EDGE,"E38"),sQuery(id+"F0.wireOp",EDGE,"E39"),sQuery(id+"F0.wireOp",EDGE,"E40.MirrorCS"),sQuery(id+"F0.wireOp",EDGE,"E41.MirrorCS"),sQuery(id+"F0.wireOp",EDGE,"E42.MirrorCS"),sQuery(id+"F0.wireOp",EDGE,"E43.MirrorCS"),sQuery(id+"F0.wireOp",EDGE,"E44.MirrorCS"),sQuery(id+"F0.wireOp",EDGE,"E45.MirrorCS"),sQuery(id+"F0.wireOp",EDGE,"E46.MirrorCS"),sQuery(id+"F0.wireOp",EDGE,"E47.MirrorCS"),sQuery(id+"F0.wireOp",EDGE,"E48.MirrorCS"),sQuery(id+"F0.wireOp",EDGE,"E49.MirrorCS"),sQuery(id+"F0.wireOp",EDGE,"E50.MirrorCS"),sQuery(id+"F0.wireOp",EDGE,"E51.MirrorCS"),sQuery(id+"F0.wireOp",EDGE,"E52.MirrorCS"),sQuery(id+"F0.wireOp",EDGE,"E53.MirrorCS"),sQuery(id+"F0.wireOp",EDGE,"E54.MirrorCS"),sQuery(id+"F0.wireOp",EDGE,"E55.MirrorCS"),sQuery(id+"F0.wireOp",EDGE,"E56.MirrorCS"),sQuery(id+"F0.wireOp",EDGE,"E57.MirrorCS"),sQuery(id+"F0.wireOp",EDGE,"E58.MirrorCS"),sQuery(id+"F0.wireOp",EDGE,"E61.MirrorCS"),sQuery(id+"F0.wireOp",EDGE,"E62.MirrorCS"),sQuery(id+"F0.wireOp",EDGE,"E63.MirrorCS"),sQuery(id+"F0.wireOp",EDGE,"E64.MirrorCS"),sQuery(id+"F0.wireOp",EDGE,"E65.MirrorCS"),sQuery(id+"F0.wireOp",EDGE,"E66.MirrorCS"),sQuery(id+"F0.wireOp",EDGE,"E67.MirrorCS"),sQuery(id+"F0.wireOp",EDGE,"E68.MirrorCS"),sQuery(id+"F0.wireOp",EDGE,"E69.MirrorCS"),sQuery(id+"F0.wireOp",EDGE,"E70.MirrorCS"),sQuery(id+"F0.wireOp",EDGE,"E71.MirrorCS"),sQuery(id+"F0.wireOp",EDGE,"E72.MirrorCS"),sQuery(id+"F0.wireOp",EDGE,"E73.MirrorCS"),sQuery(id+"F0.wireOp",EDGE,"E74.MirrorCS"),sQuery(id+"F0.wireOp",EDGE,"E75.MirrorCS"),sQuery(id+"F0.wireOp",EDGE,"E76.MirrorCS")])],"isStart":true});
            var sketch = newSketch(context, id + "F8", { "sketchPlane" : qUnion([Q0])});
            skLineSegment(sketch, "E164", {"start": v(-85.45, 90) * mm, "end": v(85.45, 90) * mm});
            skLineSegment(sketch, "E165", {"start": v(85.45, 90) * mm, "end": v(85.45, 0) * mm});
            skPoint(sketch, "E165.endSnap0", {"position": v(81.45, 0) * mm});
            skLineSegment(sketch, "E166", {"start": v(83.45, 88) * mm, "end": v(83.45, 0) * mm});
            skLineSegment(sketch, "E167", {"start": v(83.45, 88) * mm, "end": v(27.15, 88) * mm});
            skLineSegment(sketch, "E168", {"start": v(27.15, 88) * mm, "end": v(27.15, 0) * mm});
            skLineSegment(sketch, "E169", {"start": v(25.15, 0) * mm, "end": v(25.15, 88) * mm});
            skLineSegment(sketch, "E170", {"start": v(25.15, 88) * mm, "end": v(-31.15, 88) * mm});
            skLineSegment(sketch, "E171", {"start": v(-31.15, 88) * mm, "end": v(-31.15, 0) * mm});
            skLineSegment(sketch, "E172", {"start": v(-33.15, 0) * mm, "end": v(-33.15, 88) * mm});
            skLineSegment(sketch, "E173", {"start": v(-33.15, 88) * mm, "end": v(-85.45, 88) * mm});
            skLineSegment(sketch, "E174", {"start": v(-85.45, 88) * mm, "end": v(-85.45, 90) * mm});
            skLineSegment(sketch, "E175", {"start": v(-85.45, 89) * mm, "end": v(-87.45, 89) * mm, "construction": true});
            skLineSegment(sketch, "E176", {"start": v(0, 92) * mm, "end": v(0, 90) * mm, "construction": true});
            skLineSegment(sketch, "E177", {"start": v(0, 90) * mm, "end": v(0, 88) * mm, "construction": true});
            skLineSegment(sketch, "E178", {"start": v(-33.15, 44) * mm, "end": v(-31.15, 44) * mm, "construction": true});
            skLineSegment(sketch, "E179", {"start": v(-31.15, 44) * mm, "end": v(-29.15, 44) * mm, "construction": true});
            skLineSegment(sketch, "E180", {"start": v(25.15, 44) * mm, "end": v(27.15, 44) * mm, "construction": true});
            skLineSegment(sketch, "E181", {"start": v(27.15, 44) * mm, "end": v(29.15, 44) * mm, "construction": true});
            skLineSegment(sketch, "E182", {"start": v(83.45, 44) * mm, "end": v(85.45, 44) * mm, "construction": true});
            skLineSegment(sketch, "E183", {"start": v(85.45, 44) * mm, "end": v(87.45, 44) * mm, "construction": true});
            skLineSegment(sketch, "E184.MirrorCS", {"start": v(-33.15, -44) * mm, "end": v(-31.15, -44) * mm, "construction": true});
            skLineSegment(sketch, "E185.MirrorCS", {"start": v(0, -90) * mm, "end": v(0, -88) * mm, "construction": true});
            skLineSegment(sketch, "E186.MirrorCS", {"start": v(85.45, -44) * mm, "end": v(87.45, -44) * mm, "construction": true});
            skLineSegment(sketch, "E187.MirrorCS", {"start": v(25.15, -44) * mm, "end": v(27.15, -44) * mm, "construction": true});
            skLineSegment(sketch, "E188.MirrorCS", {"start": v(-85.45, -88) * mm, "end": v(-85.45, -90) * mm});
            skLineSegment(sketch, "E189.MirrorCS", {"start": v(-31.15, -44) * mm, "end": v(-29.15, -44) * mm, "construction": true});
            skLineSegment(sketch, "E190.MirrorCS", {"start": v(27.15, -44) * mm, "end": v(29.15, -44) * mm, "construction": true});
            skLineSegment(sketch, "E191.MirrorCS", {"start": v(83.45, -44) * mm, "end": v(85.45, -44) * mm, "construction": true});
            skLineSegment(sketch, "E192.MirrorCS", {"start": v(0, -92) * mm, "end": v(0, -90) * mm, "construction": true});
            skLineSegment(sketch, "E193.MirrorCS", {"start": v(-85.45, -89) * mm, "end": v(-87.45, -89) * mm, "construction": true});
            skLineSegment(sketch, "E194.MirrorCS", {"start": v(85.45, -90) * mm, "end": v(85.45, 0) * mm});
            skLineSegment(sketch, "E195.MirrorCS", {"start": v(-33.15, -88) * mm, "end": v(-85.45, -88) * mm});
            skLineSegment(sketch, "E196.MirrorCS", {"start": v(25.15, -88) * mm, "end": v(-31.15, -88) * mm});
            skLineSegment(sketch, "E197.MirrorCS", {"start": v(25.15, 0) * mm, "end": v(25.15, -88) * mm});
            skLineSegment(sketch, "E198.MirrorCS", {"start": v(-85.45, -90) * mm, "end": v(85.45, -90) * mm});
            skLineSegment(sketch, "E199.MirrorCS", {"start": v(-31.15, -88) * mm, "end": v(-31.15, 0) * mm});
            skLineSegment(sketch, "E200.MirrorCS", {"start": v(-33.15, 0) * mm, "end": v(-33.15, -88) * mm});
            skLineSegment(sketch, "E201.MirrorCS", {"start": v(83.45, -88) * mm, "end": v(27.15, -88) * mm});
            skLineSegment(sketch, "E202.MirrorCS", {"start": v(83.45, -88) * mm, "end": v(83.45, 0) * mm});
            skLineSegment(sketch, "E203.MirrorCS", {"start": v(27.15, -88) * mm, "end": v(27.15, 0) * mm});
            skSolve(sketch);
        }
        {
            var Q0;
            Q0=qSketchRegion(id+"F8",true);
            extrude(context, id + "F9", {"entities" : qUnion([Q0]), "operationType" : NewBodyOperationType.REMOVE, "oppositeDirection" : true, "depth" : 2 * mm});
        }
        {
            var Q0;
            Q0=makeQuery(id+"F1.opExtrude","SWEPT_EDGE",EDGE,{"disambiguationData":[OSD([sQuery(id+"F0.wireOp",EDGE,"E6"),sQuery(id+"F0.wireOp",EDGE,"E7")])]});
            var Q1;
            Q1=makeQuery(id+"F1.opExtrude","SWEPT_EDGE",EDGE,{"disambiguationData":[OSD([sQuery(id+"F0.wireOp",EDGE,"E37"),sQuery(id+"F0.wireOp",EDGE,"E38")])]});
            var Q2;
            Q2=makeQuery(id+"F1.opExtrude","SWEPT_EDGE",EDGE,{"disambiguationData":[OSD([sQuery(id+"F0.wireOp",EDGE,"E10"),sQuery(id+"F0.wireOp",EDGE,"E11")])]});
            var Q3;
            Q3=makeQuery(id+"F1.opExtrude","SWEPT_EDGE",EDGE,{"disambiguationData":[OSD([sQuery(id+"F0.wireOp",EDGE,"E17"),sQuery(id+"F0.wireOp",EDGE,"E18")])]});
            var Q4;
            Q4=makeQuery(id+"F1.opExtrude","SWEPT_EDGE",EDGE,{"disambiguationData":[OSD([sQuery(id+"F0.wireOp",EDGE,"E28"),sQuery(id+"F0.wireOp",EDGE,"E29")])]});
            var Q5;
            Q5=makeQuery(id+"F1.opExtrude","SWEPT_EDGE",EDGE,{"disambiguationData":[OSD([sQuery(id+"F0.wireOp",EDGE,"E21"),sQuery(id+"F0.wireOp",EDGE,"E22")])]});
            var Q6;
            Q6=makeQuery(id+"F1.opExtrude","SWEPT_EDGE",EDGE,{"disambiguationData":[OSD([sQuery(id+"F0.wireOp",EDGE,"E41.MirrorCS"),sQuery(id+"F0.wireOp",EDGE,"E73.MirrorCS")])]});
            var Q7;
            Q7=makeQuery(id+"F1.opExtrude","SWEPT_EDGE",EDGE,{"disambiguationData":[OSD([sQuery(id+"F0.wireOp",EDGE,"E52.MirrorCS"),sQuery(id+"F0.wireOp",EDGE,"E66.MirrorCS")])]});
            var Q8;
            Q8=makeQuery(id+"F1.opExtrude","SWEPT_EDGE",EDGE,{"disambiguationData":[OSD([sQuery(id+"F0.wireOp",EDGE,"E71.MirrorCS"),sQuery(id+"F0.wireOp",EDGE,"E72.MirrorCS")])]});
            var Q9;
            Q9=makeQuery(id+"F1.opExtrude","SWEPT_EDGE",EDGE,{"disambiguationData":[OSD([sQuery(id+"F0.wireOp",EDGE,"E53.MirrorCS"),sQuery(id+"F0.wireOp",EDGE,"E64.MirrorCS")])]});
            var Q10;
            Q10=makeQuery(id+"F1.opExtrude","SWEPT_EDGE",EDGE,{"disambiguationData":[OSD([sQuery(id+"F0.wireOp",EDGE,"E48.MirrorCS"),sQuery(id+"F0.wireOp",EDGE,"E68.MirrorCS")])]});
            var Q11;
            Q11=makeQuery(id+"F1.opExtrude","SWEPT_EDGE",EDGE,{"disambiguationData":[OSD([sQuery(id+"F0.wireOp",EDGE,"E42.MirrorCS"),sQuery(id+"F0.wireOp",EDGE,"E54.MirrorCS")])]});
            chamfer(context, id + "F10", {"entities" : qUnion([Q0, Q1, Q2, Q3, Q4, Q5, Q6, Q7, Q8, Q9, Q10, Q11]), "width" : 5 * mm, "tangentPropagation" : true});
        }
        {
            var Q0;
            {var subQ1=sQuery(id+"F0.wireOp",EDGE,"E58.MirrorCS");var subQ2=sQuery(id+"F0.wireOp",EDGE,"E20");var subQ4=sQuery(id+"F0.wireOp",EDGE,"E52.MirrorCS");var subQ6=sQuery(id+"F0.wireOp",EDGE,"E62.MirrorCS");var subQ7=sQuery(id+"F0.wireOp",EDGE,"E30");var subQ9=sQuery(id+"F0.wireOp",EDGE,"E40.MirrorCS");var subQ10=makeQuery(id+"F1.opExtrude","SWEPT_FACE",FACE,{"disambiguationData":[OSD([subQ9])]});var subQ12=sQuery(id+"F0.wireOp",EDGE,"E73.MirrorCS");var subQ13=sQuery(id+"F0.wireOp",EDGE,"E41.MirrorCS");var subQ16=sQuery(id+"F0.wireOp",EDGE,"E66.MirrorCS");var subQ18=sQuery(id+"F0.wireOp",EDGE,"E44.MirrorCS");var subQ22=sQuery(id+"F4.wireOp",EDGE,"E113.bottom");var subQ26=sQuery(id+"F0.wireOp",EDGE,"E23");var subQ27=sQuery(id+"F0.wireOp",EDGE,"E22");var subQ28=sQuery(id+"F0.wireOp",EDGE,"E21");var subQ29=sQuery(id+"F0.wireOp",EDGE,"E29");var subQ30=sQuery(id+"F0.wireOp",EDGE,"E27");var subQ31=sQuery(id+"F0.wireOp",EDGE,"E28");var subQ32=sQuery(id+"F4.wireOp",EDGE,"E125.MirrorCS");Q0=makeQuery(id+"F28XbOWx8GEMKOh_1.boolean.opBoolean","SPLIT",FACE,{"disambiguationData":[TD([subQ10])],"derivedFrom":makeQuery(id+"F9.boolean.opBoolean","SPLIT",FACE,{"disambiguationData":[TD([makeQuery(id+"F1.opExtrude","SWEPT_FACE",FACE,{"disambiguationData":[OSD([subQ28])]})])],"derivedFrom":makeQuery(id+"F5.boolean.opBoolean","MERGE",FACE,{"derivedFrom":[makeQuery(id+"F1.opExtrude","CAP_FACE",FACE,{"disambiguationData":[OSD([sQuery(id+"F0.wireOp",EDGE,"E0"),sQuery(id+"F0.wireOp",EDGE,"E1"),sQuery(id+"F0.wireOp",EDGE,"E2"),sQuery(id+"F0.wireOp",EDGE,"E3"),sQuery(id+"F0.wireOp",EDGE,"E4"),sQuery(id+"F0.wireOp",EDGE,"E5"),sQuery(id+"F0.wireOp",EDGE,"E6"),sQuery(id+"F0.wireOp",EDGE,"E7"),sQuery(id+"F0.wireOp",EDGE,"E8"),sQuery(id+"F0.wireOp",EDGE,"E9"),sQuery(id+"F0.wireOp",EDGE,"E10"),sQuery(id+"F0.wireOp",EDGE,"E11"),sQuery(id+"F0.wireOp",EDGE,"E12"),sQuery(id+"F0.wireOp",EDGE,"E13"),sQuery(id+"F0.wireOp",EDGE,"E14"),sQuery(id+"F0.wireOp",EDGE,"E15"),sQuery(id+"F0.wireOp",EDGE,"E16"),sQuery(id+"F0.wireOp",EDGE,"E17"),sQuery(id+"F0.wireOp",EDGE,"E18"),sQuery(id+"F0.wireOp",EDGE,"E19"),subQ2,subQ28,subQ27,subQ26,sQuery(id+"F0.wireOp",EDGE,"E24"),sQuery(id+"F0.wireOp",EDGE,"E25"),sQuery(id+"F0.wireOp",EDGE,"E26"),subQ30,subQ31,subQ29,subQ7,sQuery(id+"F0.wireOp",EDGE,"E31"),sQuery(id+"F0.wireOp",EDGE,"E37"),sQuery(id+"F0.wireOp",EDGE,"E38"),sQuery(id+"F0.wireOp",EDGE,"E39"),subQ9,subQ13,sQuery(id+"F0.wireOp",EDGE,"E42.MirrorCS"),sQuery(id+"F0.wireOp",EDGE,"E43.MirrorCS"),subQ18,sQuery(id+"F0.wireOp",EDGE,"E45.MirrorCS"),sQuery(id+"F0.wireOp",EDGE,"E46.MirrorCS"),sQuery(id+"F0.wireOp",EDGE,"E47.MirrorCS"),sQuery(id+"F0.wireOp",EDGE,"E48.MirrorCS"),sQuery(id+"F0.wireOp",EDGE,"E49.MirrorCS"),sQuery(id+"F0.wireOp",EDGE,"E50.MirrorCS"),sQuery(id+"F0.wireOp",EDGE,"E51.MirrorCS"),subQ4,sQuery(id+"F0.wireOp",EDGE,"E53.MirrorCS"),sQuery(id+"F0.wireOp",EDGE,"E54.MirrorCS"),sQuery(id+"F0.wireOp",EDGE,"E55.MirrorCS"),sQuery(id+"F0.wireOp",EDGE,"E56.MirrorCS"),sQuery(id+"F0.wireOp",EDGE,"E57.MirrorCS"),subQ1,sQuery(id+"F0.wireOp",EDGE,"E61.MirrorCS"),subQ6,sQuery(id+"F0.wireOp",EDGE,"E63.MirrorCS"),sQuery(id+"F0.wireOp",EDGE,"E64.MirrorCS"),sQuery(id+"F0.wireOp",EDGE,"E65.MirrorCS"),subQ16,sQuery(id+"F0.wireOp",EDGE,"E67.MirrorCS"),sQuery(id+"F0.wireOp",EDGE,"E68.MirrorCS"),sQuery(id+"F0.wireOp",EDGE,"E69.MirrorCS"),sQuery(id+"F0.wireOp",EDGE,"E70.MirrorCS"),sQuery(id+"F0.wireOp",EDGE,"E71.MirrorCS"),sQuery(id+"F0.wireOp",EDGE,"E72.MirrorCS"),subQ12,sQuery(id+"F0.wireOp",EDGE,"E74.MirrorCS"),sQuery(id+"F0.wireOp",EDGE,"E75.MirrorCS"),sQuery(id+"F0.wireOp",EDGE,"E76.MirrorCS")])],"isStart":true}),makeQuery(id+"F5.opExtrude","CAP_FACE",FACE,{"disambiguationData":[OSD([sQuery(id+"F4.wireOp",EDGE,"E111.bottom"),sQuery(id+"F4.wireOp",EDGE,"E111.top"),sQuery(id+"F4.wireOp",EDGE,"E111.left"),sQuery(id+"F4.wireOp",EDGE,"E111.right")])],"isStart":true}),makeQuery(id+"F5.opExtrude","CAP_FACE",FACE,{"disambiguationData":[OSD([sQuery(id+"F4.wireOp",EDGE,"E112.bottom"),sQuery(id+"F4.wireOp",EDGE,"E112.top"),sQuery(id+"F4.wireOp",EDGE,"E112.left"),sQuery(id+"F4.wireOp",EDGE,"E112.right")])],"isStart":true}),makeQuery(id+"F5.opExtrude","CAP_FACE",FACE,{"disambiguationData":[OSD([subQ22,sQuery(id+"F4.wireOp",EDGE,"E113.top"),sQuery(id+"F4.wireOp",EDGE,"E113.left"),sQuery(id+"F4.wireOp",EDGE,"E113.right")])],"isStart":true}),makeQuery(id+"F5.opExtrude","CAP_FACE",FACE,{"disambiguationData":[OSD([sQuery(id+"F4.wireOp",EDGE,"E114.MirrorCS"),sQuery(id+"F4.wireOp",EDGE,"E115.MirrorCS"),sQuery(id+"F4.wireOp",EDGE,"E117.MirrorCS"),sQuery(id+"F4.wireOp",EDGE,"E120.MirrorCS")])],"isStart":true}),makeQuery(id+"F5.opExtrude","CAP_FACE",FACE,{"disambiguationData":[OSD([sQuery(id+"F4.wireOp",EDGE,"E116.MirrorCS"),sQuery(id+"F4.wireOp",EDGE,"E122.MirrorCS"),sQuery(id+"F4.wireOp",EDGE,"E123.MirrorCS"),sQuery(id+"F4.wireOp",EDGE,"E124.MirrorCS")])],"isStart":true}),makeQuery(id+"F5.opExtrude","CAP_FACE",FACE,{"disambiguationData":[OSD([sQuery(id+"F4.wireOp",EDGE,"E118.MirrorCS"),sQuery(id+"F4.wireOp",EDGE,"E119.MirrorCS"),sQuery(id+"F4.wireOp",EDGE,"E121.MirrorCS"),subQ32])],"isStart":true})]})})});}
            var sketch = newSketch(context, id + "F11", { "sketchPlane" : qUnion([Q0])});
            skLineSegment(sketch, "E204.0", {"start": v(29.15, -86) * mm, "end": v(65.15, -86) * mm});
            skLineSegment(sketch, "E204.1", {"start": v(29.15, -86) * mm, "end": v(29.15, 86) * mm});
            skLineSegment(sketch, "E204.2", {"start": v(-29.15, -86) * mm, "end": v(6.85, -86) * mm});
            skLineSegment(sketch, "E204.3", {"start": v(-29.15, -86) * mm, "end": v(-29.15, 86) * mm});
            skLineSegment(sketch, "E205", {"start": v(4.08, -86) * mm, "end": v(-29.15, -52.77) * mm});
            skLineSegment(sketch, "E206", {"start": v(62.38, -86) * mm, "end": v(29.15, -52.77) * mm});
            skLineSegment(sketch, "E207", {"start": v(-29.15, -86) * mm, "end": v(-12.53, -69.38) * mm, "construction": true});
            skLineSegment(sketch, "E208", {"start": v(29.15, -86) * mm, "end": v(45.77, -69.38) * mm, "construction": true});
            skPoint(sketch, "E209", {"position": v(-11.15, -86) * mm});
            skCircle(sketch, "E210", {"center": v(-20.84, -77.7) * mm, "radius": 2.15 * mm});
            skCircle(sketch, "E211", {"center": v(37.46, -77.7) * mm, "radius": 2.15 * mm});
            skLineSegment(sketch, "E212.0", {"start": v(-29.15, 86) * mm, "end": v(6.85, 86) * mm});
            skLineSegment(sketch, "E212.1", {"start": v(29.15, 86) * mm, "end": v(65.15, 86) * mm});
            skLineSegment(sketch, "E213", {"start": v(-29.15, 52.77) * mm, "end": v(4.08, 86) * mm});
            skLineSegment(sketch, "E214", {"start": v(29.15, 52.77) * mm, "end": v(62.38, 86) * mm});
            skLineSegment(sketch, "E215", {"start": v(-29.15, 86) * mm, "end": v(-12.53, 69.38) * mm, "construction": true});
            skLineSegment(sketch, "E216", {"start": v(29.15, 86) * mm, "end": v(45.77, 69.38) * mm, "construction": true});
            skCircle(sketch, "E217", {"center": v(-20.84, 77.7) * mm, "radius": 2.15 * mm});
            skCircle(sketch, "E218", {"center": v(37.46, 77.7) * mm, "radius": 2.15 * mm});
            skSolve(sketch);
        }
        {
            var Q0;
            Q0=qSketchRegion(id+"F11",true);
            extrude(context, id + "F12", {"entities" : qUnion([Q0]), "operationType" : NewBodyOperationType.ADD, "oppositeDirection" : true, "depth" : 2.5 * mm});
        }
    });
